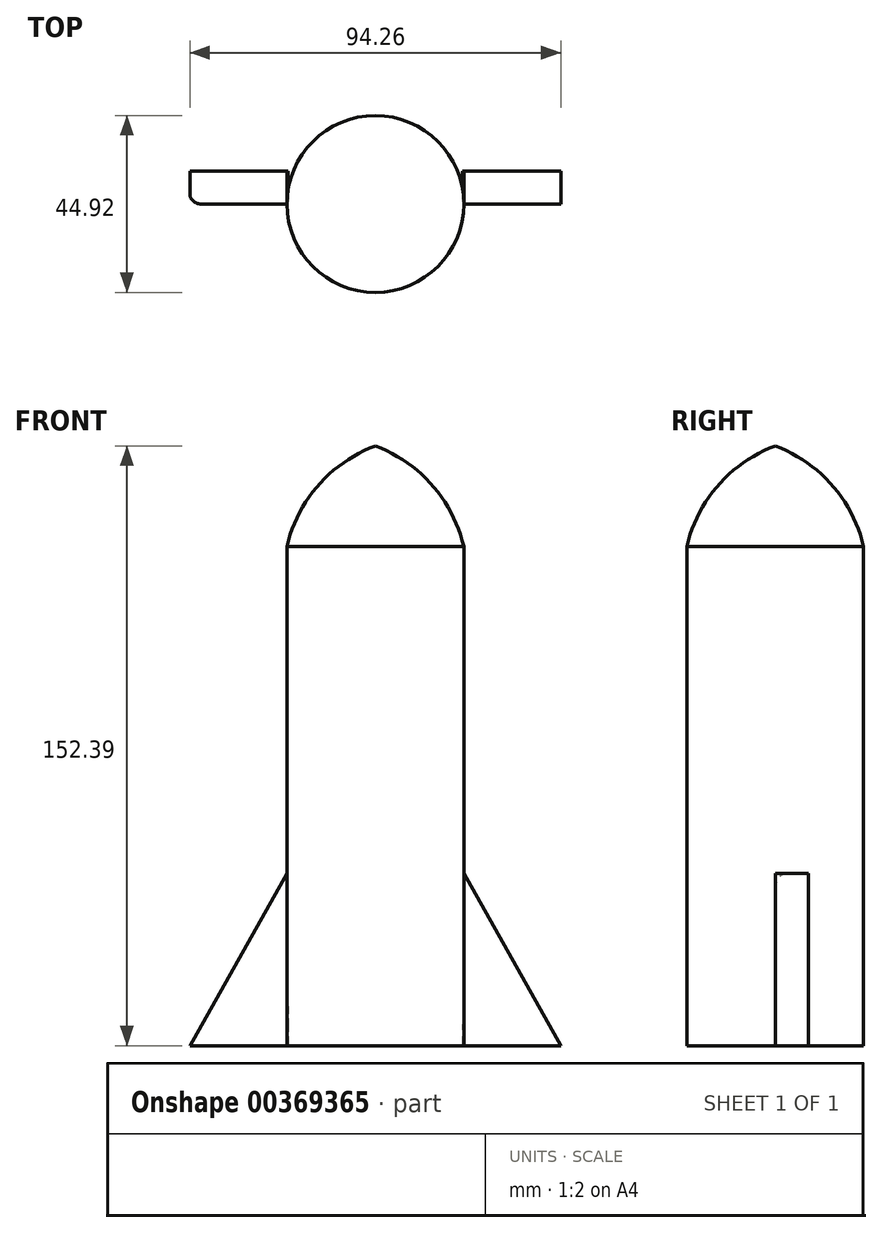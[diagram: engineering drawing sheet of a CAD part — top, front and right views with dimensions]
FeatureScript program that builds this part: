
annotation { "Feature Type Name" : "Feature", "Feature Type Description" : "" }
export const myFeature = defineFeature(function(context is Context, id is Id, definition is map)
    precondition{}
    {
        {
            var Q0;
            Q0=qCreatedBy(makeId("Front.planeOp"),FACE);
            var sketch = newSketch(context, id + "F0", { "sketchPlane" : qUnion([Q0])});
            skLineSegment(sketch, "E0", {"start": v(0, 76.34) * mm, "end": v(0, -76.05) * mm});
            skArc(sketch, "E1", {"start": v(22.46, 50.8) * mm, "mid": v(14.43, 66.38) * mm, "end": v(0, 76.34) * mm});
            skLineSegment(sketch, "E2", {"start": v(22.46, 50.8) * mm, "end": v(22.46, -76.05) * mm});
            skLineSegment(sketch, "E3", {"start": v(22.46, -76.05) * mm, "end": v(0, -76.05) * mm});
            skSolve(sketch);
        }
        {
            var Q0;
            Q0 = qSketchRegion(id + "F0", true);
            var Q1;
            Q1=sQuery(id+"F0.wireOp",EDGE,"E0");
            revolve(context, id + "F1", {"surfaceOperationType" : NewSurfaceOperationType.NEW, "entities" : qUnion([Q0]), "axis" : qUnion([Q1]), "revolveType" : RevolveType.FULL});
        }
        {
            var Q0;
            Q0=qCreatedBy(makeId("Front.planeOp"),FACE);
            var sketch = newSketch(context, id + "F2", { "sketchPlane" : qUnion([Q0])});
            skLineSegment(sketch, "E4", {"start": v(22.46, -32.3) * mm, "end": v(47.13, -76.05) * mm});
            skLineSegment(sketch, "E5", {"start": v(47.13, -76.05) * mm, "end": v(22.17, -76.05) * mm});
            skLineSegment(sketch, "E6.MirrorCS", {"start": v(-22.46, -32.3) * mm, "end": v(-47.13, -76.05) * mm});
            skLineSegment(sketch, "E7.MirrorCS", {"start": v(-47.13, -76.05) * mm, "end": v(-22.17, -76.05) * mm});
            skLineSegment(sketch, "E8", {"start": v(22.46, -32.3) * mm, "end": v(22.17, -76.05) * mm});
            skLineSegment(sketch, "E9", {"start": v(-22.46, -32.3) * mm, "end": v(-22.17, -76.05) * mm});
            skSolve(sketch);
        }
        {
            var Q0;
            Q0 = qSketchRegion(id + "F2", true);
            extrude(context, id + "F3", {"entities" : qUnion([Q0]), "oppositeDirection" : true, "depth" : 8.38 * mm, "offsetDistance" : 25.4 * mm});
        }
        {
            var Q0;
            Q0=makeQuery(id+"F3.opExtrude","CAP_EDGE",EDGE,{"disambiguationData":[OSD([sQuery(id+"F2.wireOp",EDGE,"E6.MirrorCS")])],"isStart":true});
            fillet(context, id + "F4", {"entities" : qUnion([Q0]), "radius" : 2.54 * mm, "tangentPropagation" : true, "allowEdgeOverflow" : false});
        }
    });
